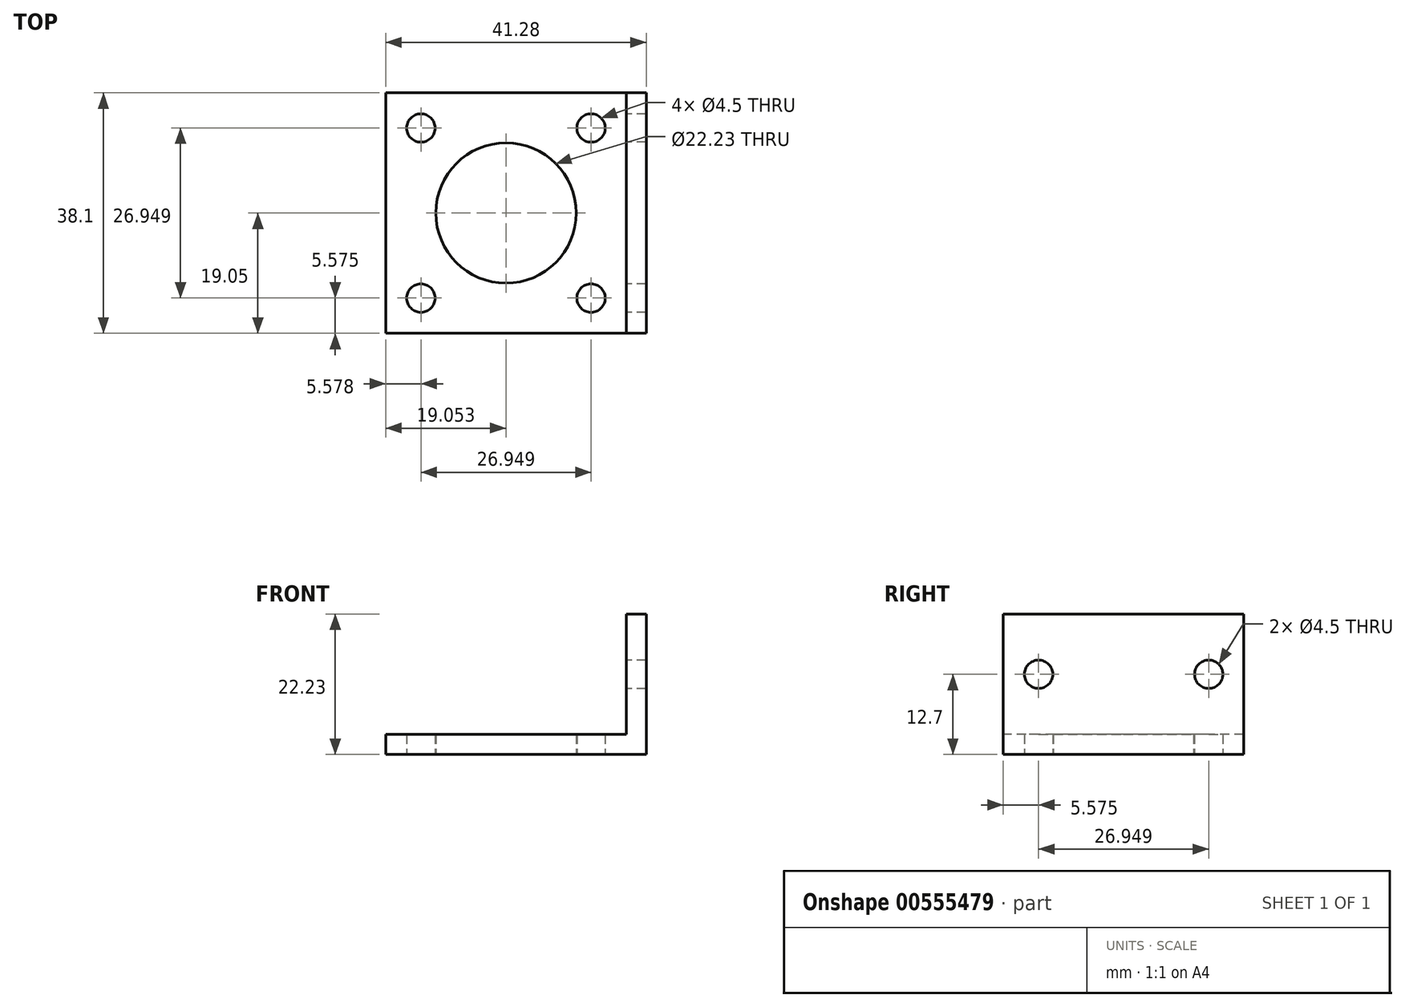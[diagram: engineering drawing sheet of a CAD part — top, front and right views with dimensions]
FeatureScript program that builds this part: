
annotation { "Feature Type Name" : "Feature", "Feature Type Description" : "" }
export const myFeature = defineFeature(function(context is Context, id is Id, definition is map)
    precondition{}
    {
        {
            var Q0;
            Q0=qCreatedBy(makeId("Top.planeOp"),FACE);
            var sketch = newSketch(context, id + "F0", { "sketchPlane" : qUnion([Q0])});
            skLineSegment(sketch, "E0.bottom", {"start": v(-20.64, 19.05) * mm, "end": v(20.64, 19.05) * mm});
            skLineSegment(sketch, "E0.top", {"start": v(-20.64, -19.05) * mm, "end": v(20.64, -19.05) * mm});
            skLineSegment(sketch, "E0.left", {"start": v(-20.64, 19.05) * mm, "end": v(-20.64, -19.05) * mm});
            skLineSegment(sketch, "E0.right", {"start": v(20.64, 19.05) * mm, "end": v(20.64, -19.05) * mm});
            skPoint(sketch, "E0.middle", {"position": v(0, 0) * mm});
            skLineSegment(sketch, "E1", {"start": v(17.46, 19.05) * mm, "end": v(17.46, -19.05) * mm});
            skLineSegment(sketch, "E2", {"start": v(-20.64, 13.47) * mm, "end": v(20.64, 13.47) * mm, "construction": true});
            skLineSegment(sketch, "E3", {"start": v(-15.06, 19.05) * mm, "end": v(-15.06, -19.05) * mm, "construction": true});
            skLineSegment(sketch, "E4", {"start": v(11.89, 19.05) * mm, "end": v(11.89, -19.05) * mm, "construction": true});
            skLineSegment(sketch, "E5", {"start": v(-20.64, -13.47) * mm, "end": v(20.64, -13.47) * mm, "construction": true});
            skLineSegment(sketch, "E6", {"start": v(-20.64, 0) * mm, "end": v(17.46, 0) * mm, "construction": true});
            skCircle(sketch, "E7", {"center": v(-1.59, 0) * mm, "radius": 11.11 * mm});
            skPoint(sketch, "E8", {"position": v(-15.06, -13.47) * mm});
            skPoint(sketch, "E9", {"position": v(-15.06, 13.47) * mm});
            skPoint(sketch, "E10", {"position": v(11.89, 13.47) * mm});
            skPoint(sketch, "E11", {"position": v(11.89, -13.47) * mm});
            skSolve(sketch);
        }
        {
            var Q0;
            {var subQ0=sQuery(id+"F0.wireOp",EDGE,"E0.right");Q0=makeQuery(id+"F0.imprint","IMPRINT",FACE,{"disambiguationData":[TD([[makeQuery(id+"F0.imprint","IMPRINT",EDGE,{"derivedFrom":subQ0}),-1.0]])]});}
            extrude(context, id + "F1", {"entities" : qUnion([Q0]), "depth" : 22.22 * mm, "offsetDistance" : 25.4 * mm});
        }
        {
            var Q0;
            {var subQ1=sQuery(id+"F0.wireOp",EDGE,"E0.left");Q0=makeQuery(id+"F0.imprint","IMPRINT",FACE,{"disambiguationData":[TD([[makeQuery(id+"F0.imprint","IMPRINT",EDGE,{"derivedFrom":subQ1}),1.0]])]});}
            extrude(context, id + "F2", {"entities" : qUnion([Q0]), "operationType" : NewBodyOperationType.ADD, "depth" : 3.17 * mm, "offsetDistance" : 25.4 * mm});
        }
        {
            var Q0;
            Q0=makeQuery(id+"F1.opExtrude","SWEPT_FACE",FACE,{"disambiguationData":[OSD([sQuery(id+"F0.wireOp",EDGE,"E1")])]});
            var sketch = newSketch(context, id + "F3", { "sketchPlane" : qUnion([Q0])});
            skPoint(sketch, "E12.endSnap0", {"position": v(-19.05, 12.7) * mm});
            skLineSegment(sketch, "E13", {"start": v(0, 22.23) * mm, "end": v(0, 3.18) * mm, "construction": true});
            skPoint(sketch, "E14", {"position": v(0, 12.7) * mm});
            skLineSegment(sketch, "E15", {"start": v(-19.05, 12.7) * mm, "end": v(19.05, 12.7) * mm, "construction": true});
            skPoint(sketch, "E16", {"position": v(-13.47, 12.7) * mm});
            skPoint(sketch, "E17", {"position": v(13.47, 12.7) * mm});
            skSolve(sketch);
        }
        {
            var Q0;
            Q0=sQuery(id+"F0.wireOp",VERTEX,"E8");
            var Q1;
            Q1=makeQuery(id+"F1.opExtrude","SWEPT_BODY",BODY,{"disambiguationData":[OSD([sQuery(id+"F0.wireOp",EDGE,"E0.bottom"),sQuery(id+"F0.wireOp",EDGE,"E0.top"),sQuery(id+"F0.wireOp",EDGE,"E0.right"),sQuery(id+"F0.wireOp",EDGE,"E1")])]});
            hole(context, id + "F4", {"style" : HoleStyle.SIMPLE, "endStyle" : HoleEndStyle.THROUGH, "oppositeDirection" : true, "standardTappedOrClearance" : lookupTablePath({ "standard" : "ANSI", "fit" : "Normal (ASME)", "size" : "#8", "type" : "Clearance" }), "standardBlindInLast" : lookupTablePath({ "fit" : "Free", "standard" : "ANSI", "size" : "#8", "type" : "Clearance" }), "holeDiameter" : 4.5 * mm, "isTappedThrough" : true, "tappedDepth" : 12.7 * mm, "tapClearance" : 3, "locations" : qUnion([Q0]), "scope" : qUnion([Q1])});
        }
        {
            var Q0;
            Q0=sQuery(id+"F0.wireOp",VERTEX,"E9");
            var Q1;
            Q1=makeQuery(id+"F1.opExtrude","SWEPT_BODY",BODY,{"disambiguationData":[OSD([sQuery(id+"F0.wireOp",EDGE,"E0.bottom"),sQuery(id+"F0.wireOp",EDGE,"E0.top"),sQuery(id+"F0.wireOp",EDGE,"E0.right"),sQuery(id+"F0.wireOp",EDGE,"E1")])]});
            hole(context, id + "F5", {"style" : HoleStyle.SIMPLE, "endStyle" : HoleEndStyle.THROUGH, "oppositeDirection" : true, "standardTappedOrClearance" : lookupTablePath({ "standard" : "ANSI", "fit" : "Normal (ASME)", "size" : "#8", "type" : "Clearance" }), "standardBlindInLast" : lookupTablePath({ "fit" : "Free", "standard" : "ANSI", "size" : "#8", "type" : "Clearance" }), "holeDiameter" : 4.5 * mm, "isTappedThrough" : true, "tappedDepth" : 12.7 * mm, "tapClearance" : 3, "locations" : qUnion([Q0]), "scope" : qUnion([Q1])});
        }
        {
            var Q0;
            Q0=sQuery(id+"F0.wireOp",VERTEX,"E10");
            var Q1;
            Q1=makeQuery(id+"F1.opExtrude","SWEPT_BODY",BODY,{"disambiguationData":[OSD([sQuery(id+"F0.wireOp",EDGE,"E0.bottom"),sQuery(id+"F0.wireOp",EDGE,"E0.top"),sQuery(id+"F0.wireOp",EDGE,"E0.right"),sQuery(id+"F0.wireOp",EDGE,"E1")])]});
            hole(context, id + "F6", {"style" : HoleStyle.SIMPLE, "endStyle" : HoleEndStyle.THROUGH, "oppositeDirection" : true, "standardTappedOrClearance" : lookupTablePath({ "standard" : "ANSI", "fit" : "Normal (ASME)", "size" : "#8", "type" : "Clearance" }), "standardBlindInLast" : lookupTablePath({ "fit" : "Free", "standard" : "ANSI", "size" : "#8", "type" : "Clearance" }), "holeDiameter" : 4.5 * mm, "isTappedThrough" : true, "tappedDepth" : 12.7 * mm, "tapClearance" : 3, "locations" : qUnion([Q0]), "scope" : qUnion([Q1])});
        }
        {
            var Q0;
            Q0=sQuery(id+"F0.wireOp",VERTEX,"E11");
            var Q1;
            Q1=makeQuery(id+"F1.opExtrude","SWEPT_BODY",BODY,{"disambiguationData":[OSD([sQuery(id+"F0.wireOp",EDGE,"E0.bottom"),sQuery(id+"F0.wireOp",EDGE,"E0.top"),sQuery(id+"F0.wireOp",EDGE,"E0.right"),sQuery(id+"F0.wireOp",EDGE,"E1")])]});
            hole(context, id + "F7", {"style" : HoleStyle.SIMPLE, "endStyle" : HoleEndStyle.THROUGH, "oppositeDirection" : true, "standardTappedOrClearance" : lookupTablePath({ "standard" : "ANSI", "fit" : "Normal (ASME)", "size" : "#8", "type" : "Clearance" }), "standardBlindInLast" : lookupTablePath({ "fit" : "Free", "standard" : "ANSI", "size" : "#8", "type" : "Clearance" }), "holeDiameter" : 4.5 * mm, "isTappedThrough" : true, "tappedDepth" : 12.7 * mm, "tapClearance" : 3, "locations" : qUnion([Q0]), "scope" : qUnion([Q1])});
        }
        {
            var Q0;
            Q0=sQuery(id+"F3.wireOp",VERTEX,"E16");
            var Q1;
            Q1=makeQuery(id+"F1.opExtrude","SWEPT_BODY",BODY,{"disambiguationData":[OSD([sQuery(id+"F0.wireOp",EDGE,"E0.bottom"),sQuery(id+"F0.wireOp",EDGE,"E0.top"),sQuery(id+"F0.wireOp",EDGE,"E0.right"),sQuery(id+"F0.wireOp",EDGE,"E1")])]});
            hole(context, id + "F8", {"style" : HoleStyle.SIMPLE, "endStyle" : HoleEndStyle.THROUGH, "standardTappedOrClearance" : lookupTablePath({ "standard" : "ANSI", "fit" : "Normal (ASME)", "size" : "#8", "type" : "Clearance" }), "standardBlindInLast" : lookupTablePath({ "fit" : "Free", "standard" : "ANSI", "size" : "#8", "type" : "Clearance" }), "holeDiameter" : 4.5 * mm, "isTappedThrough" : true, "tappedDepth" : 12.7 * mm, "tapClearance" : 3, "locations" : qUnion([Q0]), "scope" : qUnion([Q1])});
        }
        {
            var Q0;
            Q0=sQuery(id+"F3.wireOp",VERTEX,"E17");
            var Q1;
            Q1=makeQuery(id+"F1.opExtrude","SWEPT_BODY",BODY,{"disambiguationData":[OSD([sQuery(id+"F0.wireOp",EDGE,"E0.bottom"),sQuery(id+"F0.wireOp",EDGE,"E0.top"),sQuery(id+"F0.wireOp",EDGE,"E0.right"),sQuery(id+"F0.wireOp",EDGE,"E1")])]});
            hole(context, id + "F9", {"style" : HoleStyle.SIMPLE, "endStyle" : HoleEndStyle.THROUGH, "standardTappedOrClearance" : lookupTablePath({ "standard" : "ANSI", "fit" : "Normal (ASME)", "size" : "#8", "type" : "Clearance" }), "standardBlindInLast" : lookupTablePath({ "fit" : "Free", "standard" : "ANSI", "size" : "#8", "type" : "Clearance" }), "holeDiameter" : 4.5 * mm, "isTappedThrough" : true, "tappedDepth" : 12.7 * mm, "tapClearance" : 3, "locations" : qUnion([Q0]), "scope" : qUnion([Q1])});
        }
    });
